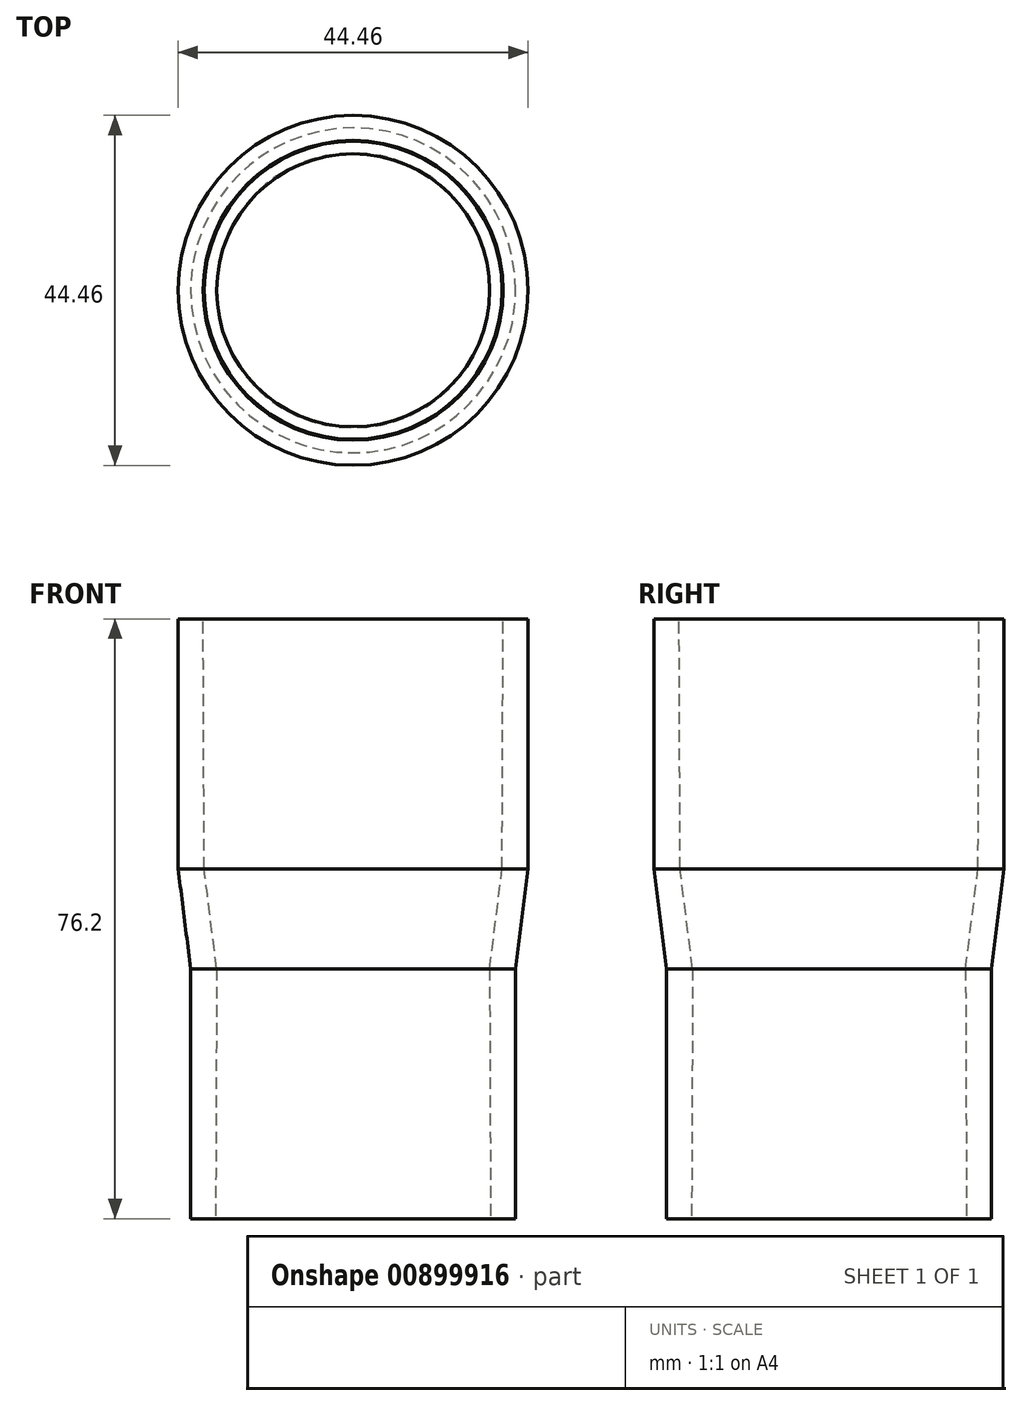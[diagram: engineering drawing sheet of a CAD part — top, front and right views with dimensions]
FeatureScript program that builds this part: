
annotation { "Feature Type Name" : "Feature", "Feature Type Description" : "" }
export const myFeature = defineFeature(function(context is Context, id is Id, definition is map)
    precondition{}
    {
        {
            var Q0;
            Q0=qCreatedBy(makeId("Front.planeOp"),FACE);
            var sketch = newSketch(context, id + "F0", { "sketchPlane" : qUnion([Q0])});
            skLineSegment(sketch, "E0", {"start": v(17.46, 0) * mm, "end": v(17.34, 31.75) * mm});
            skLineSegment(sketch, "E1", {"start": v(17.34, 31.75) * mm, "end": v(18.92, 44.45) * mm});
            skLineSegment(sketch, "E2", {"start": v(18.92, 44.45) * mm, "end": v(19.05, 76.2) * mm});
            skLineSegment(sketch, "E3", {"start": v(19.05, 76.2) * mm, "end": v(22.22, 76.2) * mm});
            skLineSegment(sketch, "E4", {"start": v(20.64, 0) * mm, "end": v(17.46, 0) * mm});
            skLineSegment(sketch, "E5", {"start": v(22.22, 76.2) * mm, "end": v(22.22, 44.45) * mm});
            skLineSegment(sketch, "E6", {"start": v(22.22, 44.45) * mm, "end": v(20.64, 31.75) * mm});
            skLineSegment(sketch, "E7", {"start": v(20.64, 0) * mm, "end": v(20.64, 31.75) * mm});
            skLineSegment(sketch, "E8", {"start": v(0, 0) * mm, "end": v(0, 85.58) * mm, "construction": true});
            skSolve(sketch);
        }
        {
            var Q0;
            Q0 = qSketchRegion(id + "F0", true);
            var Q1;
            Q1=sQuery(id+"F0.wireOp",EDGE,"E8");
            revolve(context, id + "F1", {"surfaceOperationType" : NewSurfaceOperationType.NEW, "entities" : qUnion([Q0]), "axis" : qUnion([Q1]), "revolveType" : RevolveType.FULL});
        }
    });
